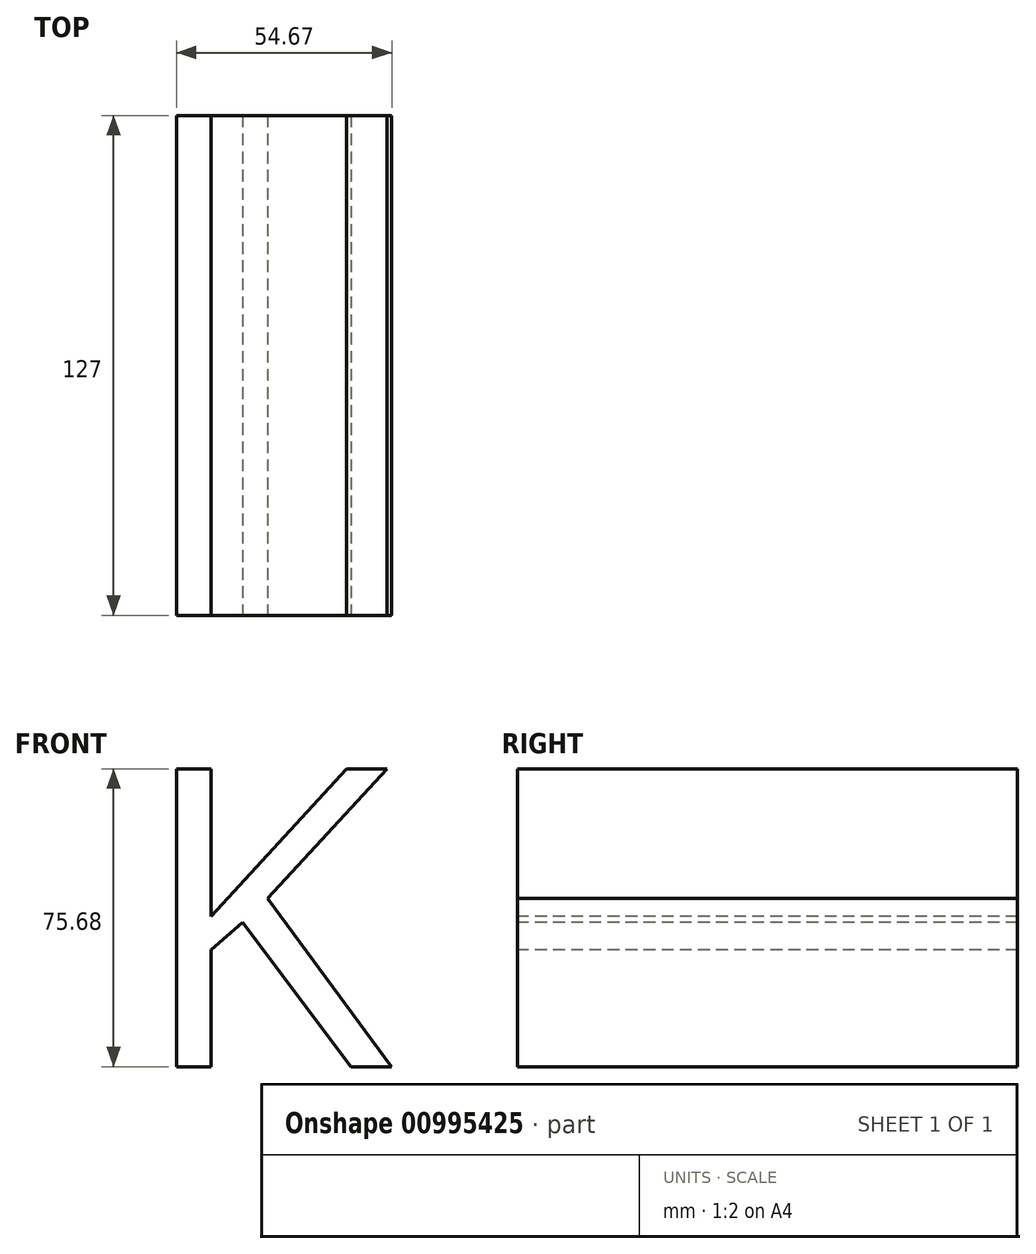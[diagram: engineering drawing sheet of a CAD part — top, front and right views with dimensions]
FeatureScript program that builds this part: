
annotation { "Feature Type Name" : "Feature", "Feature Type Description" : "" }
export const myFeature = defineFeature(function(context is Context, id is Id, definition is map)
    precondition{}
    {
        {
            var Q0;
            Q0=qCreatedBy(makeId("Front.planeOp"),FACE);
            var sketch = newSketch(context, id + "F0", { "sketchPlane" : qUnion([Q0])});
            skText(sketch, "E0", { "text": "K", "fontName": "OpenSans-Regular.ttf"});
            const initialGuessF0  = {"E0": [-0.02842, -0.04136, 1, 0, 0.07633]};
            skSetInitialGuess(sketch, initialGuessF0);
            skSolve(sketch);
        }
        {
            var Q0;
            Q0 = qSketchRegion(id + "F0", true);
            var Q1;
            Q1 = qConstructionFilter(qBodyType(qCreatedBy(id + "F0" ,EDGE), BodyType.WIRE), ConstructionObject.NO);
            extrude(context, id + "F1", {"entities" : qUnion([Q0]), "bodyType" : ToolBodyType.SURFACE, "surfaceEntities" : qUnion([Q1]), "depth" : 127 * mm, "offsetDistance" : 25.4 * mm});
        }
    });
